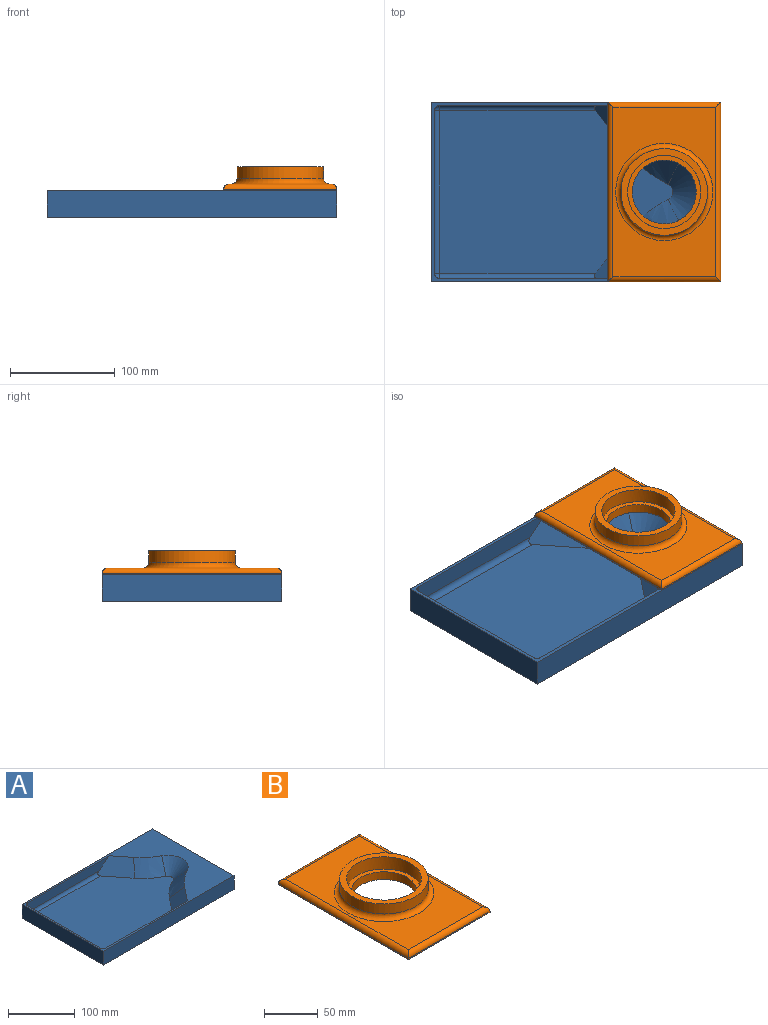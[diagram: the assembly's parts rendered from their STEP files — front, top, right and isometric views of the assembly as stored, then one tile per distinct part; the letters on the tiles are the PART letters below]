
ASSEMBLY  parts=2 mates=1
PART A: 22 faces, bbox 280.6x175.8x38.9 mm
  f0: plane 279.45x174.68mm, normal (0,0,1), area 11768.7mm2, adj f1,f2,f3,f4,f6,f7,f8,f9
  f1: plane 276.23x25.4mm, normal (0,-1,0), area 7016.1mm2, adj f0,f2,f4,f5
  f2: plane 171.45x25.4mm, normal (1,0,0), area 4354.8mm2, adj f0,f1,f3,f5
  f3: plane 276.23x25.4mm, normal (0,1,0), area 7016.1mm2, adj f0,f2,f4,f5
  f4: plane 171.45x25.4mm, normal (-1,0,0), area 4354.8mm2, adj f0,f1,f3,f5
  f5: plane 276.23x171.45mm, normal (0,0,-1), area 47358.8mm2, adj f1,f2,f3,f4
  f6: plane 52.49x50.65mm, normal (-0.55,-0.44,0.71), area 1490.2mm2, adj f0,f7,f12,f14,f18
  f7: plane 172.72x17.15mm, normal (0,-1,0), area 2773.7mm2, adj f0,f6,f18,f21
  f8: plane 154.94x17.15mm, normal (1,0,0), area 2656.4mm2, adj f0,f16,f19,f21
  f9: plane 172.72x17.15mm, normal (0,1,0), area 2773.7mm2, adj f0,f10,f15,f16
  f10: plane 52.49x50.65mm, normal (-0.55,0.44,0.71), area 1490.2mm2, adj f0,f9,f12,f13,f15
  f11: cone r=30.48mm half-angle=45deg, axis (0,0,1), area 1350.7mm2, adj f0,f12,f13,f14
  f12: plane 226.16x158.85mm, normal (0,0,1), area 28182mm2, adj f6,f10,f11,f13,f14,f15,f18,f19
  f13: bspline ~53.87x51.87mm, area 1399.9mm2, adj f0,f10,f11,f12
  f14: bspline ~53.87x51.87mm, area 1399.9mm2, adj f0,f6,f11,f12
  f15: cylinder r=5.08mm len=150.84mm, axis (1,0,0), area 1193.9mm2, adj f9,f10,f12,f17
  f16: cylinder r=5.08mm len=17.15mm, axis (0,0,-1), area 136.8mm2, adj f0,f8,f9,f17
  f17: sphere r=5.08mm, area 40.5mm2, adj f15,f16,f19
  f18: cylinder r=5.08mm len=150.84mm, axis (-1,0,0), area 1193.9mm2, adj f6,f7,f12,f20
  f19: cylinder r=5.08mm len=154.94mm, axis (0,-1,0), area 1236.4mm2, adj f8,f12,f17,f20
  f20: sphere r=5.08mm, area 70mm2, adj f18,f19,f21
  f21: cylinder r=5.08mm len=17.15mm, axis (0,0,1), area 136.8mm2, adj f0,f7,f8,f20
PART B: 16 faces, bbox 108.2x171.5x22.9 mm
  f0: plane 107.95x1.27mm, normal (0,-1,0), area 137.1mm2, adj f1,f3,f5,f12
  f1: plane 171.45x1.27mm, normal (1,0,0), area 217.7mm2, adj f0,f2,f5,f13
  f2: plane 107.95x1.27mm, normal (0,1,0), area 137.1mm2, adj f1,f3,f5,f15
  f3: plane 171.45x1.27mm, normal (-1,0,0), area 217.7mm2, adj f0,f2,f5,f14
  f4: plane 161.29x97.79mm, normal (0,0,1), area 9021.9mm2, adj f11,f12,f13,f14,f15
  f5: plane 171.45x107.95mm, normal (0,0,-1), area 15589.4mm2, adj f0,f1,f2,f3,f9
  f6: cylinder r=34.92mm len=69.85mm, axis (0,0,-1), area 3065.6mm2, adj f8,f10
  f7: cylinder r=41.27mm len=82.55mm, axis (0,0,-1), area 2964.2mm2, adj f8,f11
  f8: plane 82.55x82.55mm, normal (0,0,1), area 1520.1mm2, adj f6,f7
  f9: cylinder r=30.48mm len=60.96mm, axis (0,0,-1), area 1702.5mm2, adj f5,f10
  f10: plane 69.85x69.85mm, normal (0,0,1), area 913.3mm2, adj f6,f9
  f11: torus R=46.35mm, axis (0,0,1), area 2162mm2, adj f4,f7
  f12: cylinder r=5.08mm len=107.95mm, axis (-1,0,0), area 831.9mm2, adj f0,f4,f13,f14
  f13: cylinder r=5.08mm len=171.45mm, axis (0,-1,0), area 1338.6mm2, adj f1,f4,f12,f15
  f14: cylinder r=5.08mm len=171.45mm, axis (0,1,0), area 1338.6mm2, adj f3,f4,f12,f15
  f15: cylinder r=5.08mm len=107.95mm, axis (1,0,0), area 831.9mm2, adj f2,f4,f13,f14
PLACE A t=(-62.9,-8.47,29.07)mm
PLACE B t=(21.24,-8.47,54.47)mm
MATE fastened B.f6 <-> A.f11  axis (0,0,-1) through (21.24,-8.47,54.47)mm
